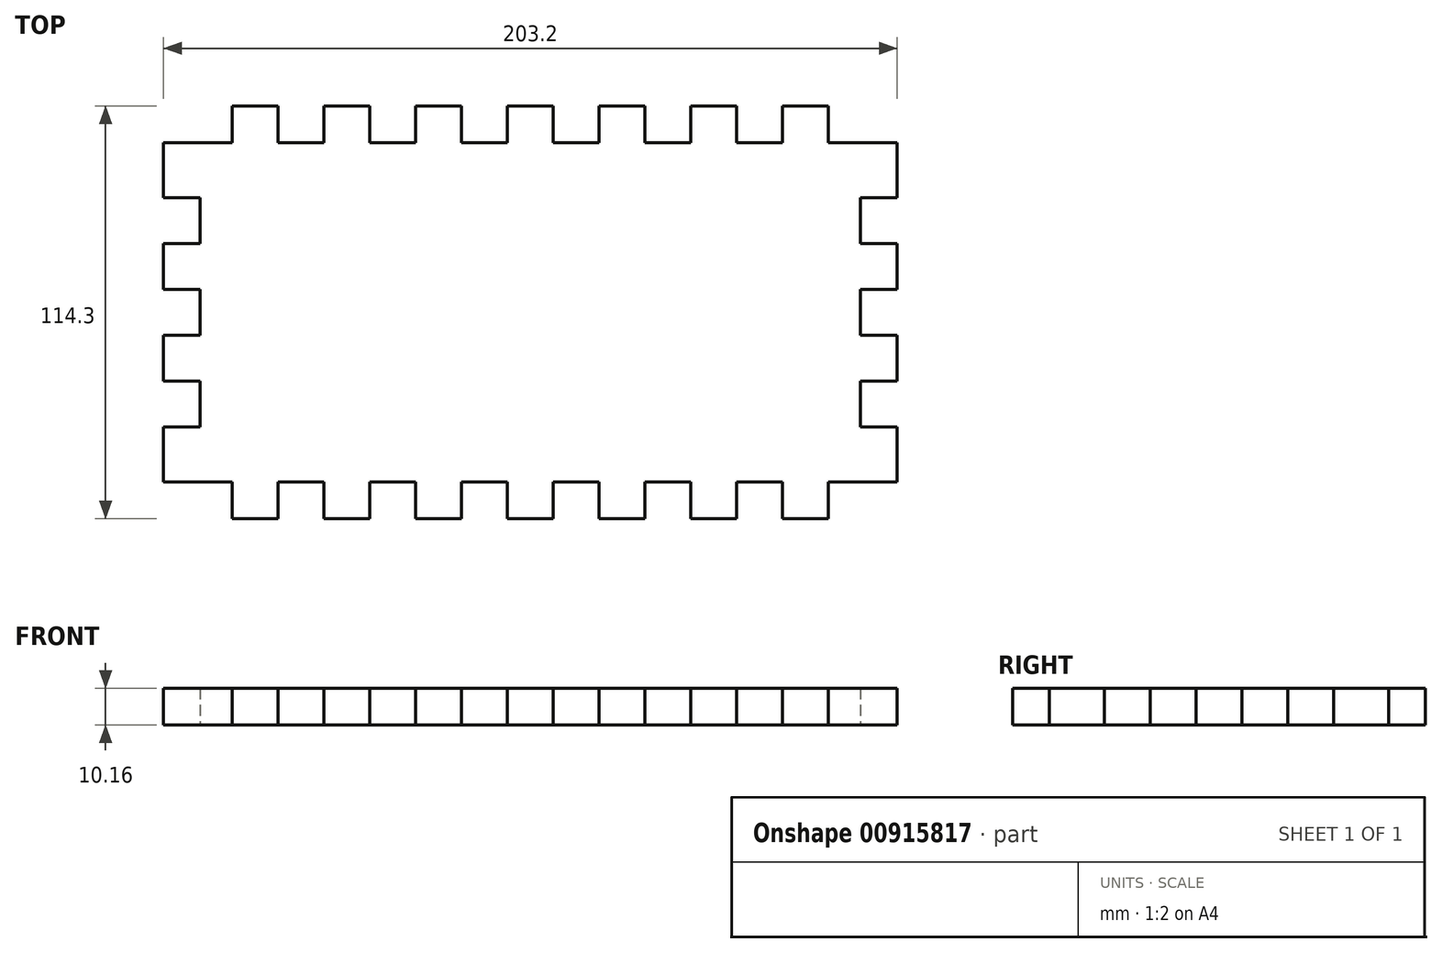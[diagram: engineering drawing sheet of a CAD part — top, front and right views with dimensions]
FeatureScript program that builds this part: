
annotation { "Feature Type Name" : "Feature", "Feature Type Description" : "" }
export const myFeature = defineFeature(function(context is Context, id is Id, definition is map)
    precondition{}
    {
        {
            var Q0;
            Q0=qCreatedBy(makeId("Top.planeOp"),FACE);
            var sketch = newSketch(context, id + "F0", { "sketchPlane" : qUnion([Q0])});
            skLineSegment(sketch, "E0.bottom", {"start": v(19.05, 0) * mm, "end": v(31.75, 0) * mm});
            skLineSegment(sketch, "E0.left", {"start": v(0, -10.16) * mm, "end": v(0, -25.4) * mm});
            skLineSegment(sketch, "E1", {"start": v(0, -10.16) * mm, "end": v(19.05, -10.16) * mm});
            skLineSegment(sketch, "E2", {"start": v(19.05, -10.16) * mm, "end": v(19.05, 0) * mm});
            skLineSegment(sketch, "E3", {"start": v(31.75, 0) * mm, "end": v(31.75, -10.16) * mm});
            skLineSegment(sketch, "E4", {"start": v(31.75, -10.16) * mm, "end": v(44.45, -10.16) * mm});
            skLineSegment(sketch, "E5", {"start": v(44.45, -10.16) * mm, "end": v(44.45, 0) * mm});
            skLineSegment(sketch, "E6", {"start": v(44.45, 0) * mm, "end": v(57.15, 0) * mm});
            skLineSegment(sketch, "E7", {"start": v(57.15, 0) * mm, "end": v(57.15, -10.16) * mm});
            skLineSegment(sketch, "E8", {"start": v(57.15, -10.16) * mm, "end": v(69.85, -10.16) * mm});
            skLineSegment(sketch, "E9", {"start": v(69.85, -10.16) * mm, "end": v(69.85, 0) * mm});
            skLineSegment(sketch, "E10", {"start": v(69.85, 0) * mm, "end": v(82.55, 0) * mm});
            skLineSegment(sketch, "E11", {"start": v(82.55, 0) * mm, "end": v(82.55, -10.16) * mm});
            skLineSegment(sketch, "E12", {"start": v(82.55, -10.16) * mm, "end": v(95.25, -10.16) * mm});
            skLineSegment(sketch, "E13", {"start": v(95.25, -10.16) * mm, "end": v(95.25, 0) * mm});
            skPoint(sketch, "E14.orphan", {"position": v(0, 0) * mm});
            skLineSegment(sketch, "E15.trimOffspring", {"start": v(95.25, 0) * mm, "end": v(107.95, 0) * mm});
            skLineSegment(sketch, "E16", {"start": v(107.95, 0) * mm, "end": v(107.95, -10.16) * mm});
            skLineSegment(sketch, "E17", {"start": v(107.95, -10.16) * mm, "end": v(120.65, -10.16) * mm});
            skLineSegment(sketch, "E18", {"start": v(120.65, -10.16) * mm, "end": v(120.65, 0) * mm});
            skLineSegment(sketch, "E19", {"start": v(120.65, 0) * mm, "end": v(133.35, 0) * mm});
            skLineSegment(sketch, "E20", {"start": v(133.35, 0) * mm, "end": v(133.35, -10.16) * mm});
            skLineSegment(sketch, "E21", {"start": v(133.35, -10.16) * mm, "end": v(146.05, -10.16) * mm});
            skLineSegment(sketch, "E22", {"start": v(146.05, -10.16) * mm, "end": v(146.05, 0) * mm});
            skLineSegment(sketch, "E23", {"start": v(146.05, 0) * mm, "end": v(158.75, 0) * mm});
            skLineSegment(sketch, "E24", {"start": v(158.75, 0) * mm, "end": v(158.75, -10.16) * mm});
            skLineSegment(sketch, "E25", {"start": v(158.75, -10.16) * mm, "end": v(171.45, -10.16) * mm});
            skLineSegment(sketch, "E26", {"start": v(171.45, -10.16) * mm, "end": v(171.45, 0) * mm});
            skLineSegment(sketch, "E27.trimOffspring", {"start": v(171.45, 0) * mm, "end": v(184.15, 0) * mm});
            skLineSegment(sketch, "E28", {"start": v(184.15, 0) * mm, "end": v(184.15, -10.16) * mm});
            skLineSegment(sketch, "E29", {"start": v(184.15, -10.16) * mm, "end": v(203.2, -10.16) * mm});
            skPoint(sketch, "E30.orphan", {"position": v(203.2, 0) * mm});
            skLineSegment(sketch, "E31", {"start": v(0, -25.4) * mm, "end": v(10.16, -25.4) * mm});
            skLineSegment(sketch, "E32", {"start": v(10.16, -25.4) * mm, "end": v(10.16, -38.1) * mm});
            skLineSegment(sketch, "E33", {"start": v(10.16, -38.1) * mm, "end": v(0, -38.1) * mm});
            skLineSegment(sketch, "E34", {"start": v(0, -38.1) * mm, "end": v(0, -50.8) * mm});
            skLineSegment(sketch, "E35", {"start": v(0, -50.8) * mm, "end": v(10.16, -50.8) * mm});
            skLineSegment(sketch, "E36", {"start": v(10.16, -50.8) * mm, "end": v(10.16, -63.5) * mm});
            skLineSegment(sketch, "E37", {"start": v(10.16, -63.5) * mm, "end": v(0, -63.5) * mm});
            skLineSegment(sketch, "E38", {"start": v(0, -63.5) * mm, "end": v(0, -76.2) * mm});
            skLineSegment(sketch, "E39", {"start": v(0, -76.2) * mm, "end": v(10.16, -76.2) * mm});
            skLineSegment(sketch, "E40", {"start": v(10.16, -76.2) * mm, "end": v(10.16, -88.9) * mm});
            skLineSegment(sketch, "E41", {"start": v(10.16, -88.9) * mm, "end": v(0, -88.9) * mm});
            skLineSegment(sketch, "E42.trimOffspring", {"start": v(0, -88.9) * mm, "end": v(0, -104.14) * mm});
            skLineSegment(sketch, "E43", {"start": v(0, -104.14) * mm, "end": v(19.05, -104.14) * mm});
            skLineSegment(sketch, "E44", {"start": v(19.05, -104.14) * mm, "end": v(19.05, -114.3) * mm});
            skPoint(sketch, "E45.orphan", {"position": v(0, -114.3) * mm});
            skLineSegment(sketch, "E46", {"start": v(101.6, 0) * mm, "end": v(101.6, 0) * mm});
            skLineSegment(sketch, "E47", {"start": v(10.16, -57.15) * mm, "end": v(10.16, -57.15) * mm});
            skLineSegment(sketch, "E48.MirrorCS", {"start": v(203.2, -10.16) * mm, "end": v(203.2, -25.4) * mm});
            skLineSegment(sketch, "E49.MirrorCS", {"start": v(203.2, -25.4) * mm, "end": v(193.04, -25.4) * mm});
            skLineSegment(sketch, "E50.MirrorCS", {"start": v(193.04, -25.4) * mm, "end": v(193.04, -38.1) * mm});
            skLineSegment(sketch, "E51.MirrorCS", {"start": v(193.04, -38.1) * mm, "end": v(203.2, -38.1) * mm});
            skLineSegment(sketch, "E52.MirrorCS", {"start": v(203.2, -38.1) * mm, "end": v(203.2, -50.8) * mm});
            skLineSegment(sketch, "E53.MirrorCS", {"start": v(203.2, -50.8) * mm, "end": v(193.04, -50.8) * mm});
            skLineSegment(sketch, "E54.MirrorCS", {"start": v(193.04, -50.8) * mm, "end": v(193.04, -63.5) * mm});
            skLineSegment(sketch, "E55.MirrorCS", {"start": v(193.04, -63.5) * mm, "end": v(203.2, -63.5) * mm});
            skLineSegment(sketch, "E56.MirrorCS", {"start": v(203.2, -63.5) * mm, "end": v(203.2, -76.2) * mm});
            skLineSegment(sketch, "E57.MirrorCS", {"start": v(203.2, -76.2) * mm, "end": v(193.04, -76.2) * mm});
            skLineSegment(sketch, "E58.MirrorCS", {"start": v(193.04, -76.2) * mm, "end": v(193.04, -88.9) * mm});
            skLineSegment(sketch, "E59.MirrorCS", {"start": v(193.04, -88.9) * mm, "end": v(203.2, -88.9) * mm});
            skLineSegment(sketch, "E60.MirrorCS", {"start": v(203.2, -88.9) * mm, "end": v(203.2, -104.14) * mm});
            skLineSegment(sketch, "E61.MirrorCS", {"start": v(203.2, -104.14) * mm, "end": v(184.15, -104.14) * mm});
            skLineSegment(sketch, "E62.MirrorCS", {"start": v(184.15, -104.14) * mm, "end": v(184.15, -114.3) * mm});
            skLineSegment(sketch, "E63.MirrorCS", {"start": v(19.05, -114.3) * mm, "end": v(31.75, -114.3) * mm});
            skLineSegment(sketch, "E64.MirrorCS", {"start": v(31.75, -114.3) * mm, "end": v(31.75, -104.14) * mm});
            skLineSegment(sketch, "E65.MirrorCS", {"start": v(31.75, -104.14) * mm, "end": v(44.45, -104.14) * mm});
            skLineSegment(sketch, "E66.MirrorCS", {"start": v(44.45, -104.14) * mm, "end": v(44.45, -114.3) * mm});
            skLineSegment(sketch, "E67.MirrorCS", {"start": v(44.45, -114.3) * mm, "end": v(57.15, -114.3) * mm});
            skLineSegment(sketch, "E68.MirrorCS", {"start": v(57.15, -114.3) * mm, "end": v(57.15, -104.14) * mm});
            skLineSegment(sketch, "E69.MirrorCS", {"start": v(57.15, -104.14) * mm, "end": v(69.85, -104.14) * mm});
            skLineSegment(sketch, "E70.MirrorCS", {"start": v(69.85, -104.14) * mm, "end": v(69.85, -114.3) * mm});
            skLineSegment(sketch, "E71.MirrorCS", {"start": v(69.85, -114.3) * mm, "end": v(82.55, -114.3) * mm});
            skLineSegment(sketch, "E72.MirrorCS", {"start": v(82.55, -114.3) * mm, "end": v(82.55, -104.14) * mm});
            skLineSegment(sketch, "E73.MirrorCS", {"start": v(82.55, -104.14) * mm, "end": v(95.25, -104.14) * mm});
            skLineSegment(sketch, "E74.MirrorCS", {"start": v(95.25, -104.14) * mm, "end": v(95.25, -114.3) * mm});
            skLineSegment(sketch, "E75.MirrorCS", {"start": v(95.25, -114.3) * mm, "end": v(107.95, -114.3) * mm});
            skLineSegment(sketch, "E76.MirrorCS", {"start": v(107.95, -114.3) * mm, "end": v(107.95, -104.14) * mm});
            skLineSegment(sketch, "E77.MirrorCS", {"start": v(107.95, -104.14) * mm, "end": v(120.65, -104.14) * mm});
            skLineSegment(sketch, "E78.MirrorCS", {"start": v(120.65, -104.14) * mm, "end": v(120.65, -114.3) * mm});
            skLineSegment(sketch, "E79.MirrorCS", {"start": v(120.65, -114.3) * mm, "end": v(133.35, -114.3) * mm});
            skLineSegment(sketch, "E80.MirrorCS", {"start": v(133.35, -114.3) * mm, "end": v(133.35, -104.14) * mm});
            skLineSegment(sketch, "E81.MirrorCS", {"start": v(133.35, -104.14) * mm, "end": v(146.05, -104.14) * mm});
            skLineSegment(sketch, "E82.MirrorCS", {"start": v(146.05, -104.14) * mm, "end": v(146.05, -114.3) * mm});
            skLineSegment(sketch, "E83.MirrorCS", {"start": v(146.05, -114.3) * mm, "end": v(158.75, -114.3) * mm});
            skLineSegment(sketch, "E84.MirrorCS", {"start": v(158.75, -114.3) * mm, "end": v(158.75, -104.14) * mm});
            skLineSegment(sketch, "E85.MirrorCS", {"start": v(158.75, -104.14) * mm, "end": v(171.45, -104.14) * mm});
            skLineSegment(sketch, "E86.MirrorCS", {"start": v(171.45, -104.14) * mm, "end": v(171.45, -114.3) * mm});
            skLineSegment(sketch, "E87.MirrorCS", {"start": v(171.45, -114.3) * mm, "end": v(184.15, -114.3) * mm});
            skSolve(sketch);
        }
        {
            var Q0;
            Q0=makeQuery(id+"F0.imprint","IMPRINT",FACE,{"disambiguationData":[TD([[makeQuery(id+"F0.imprint","IMPRINT",EDGE,{"derivedFrom":sQuery(id+"F0.wireOp",EDGE,"E1")}),-1.0]])]});
            extrude(context, id + "F1", {"entities" : qUnion([Q0]), "depth" : 10.16 * mm, "offsetDistance" : 25.4 * mm});
        }
    });
